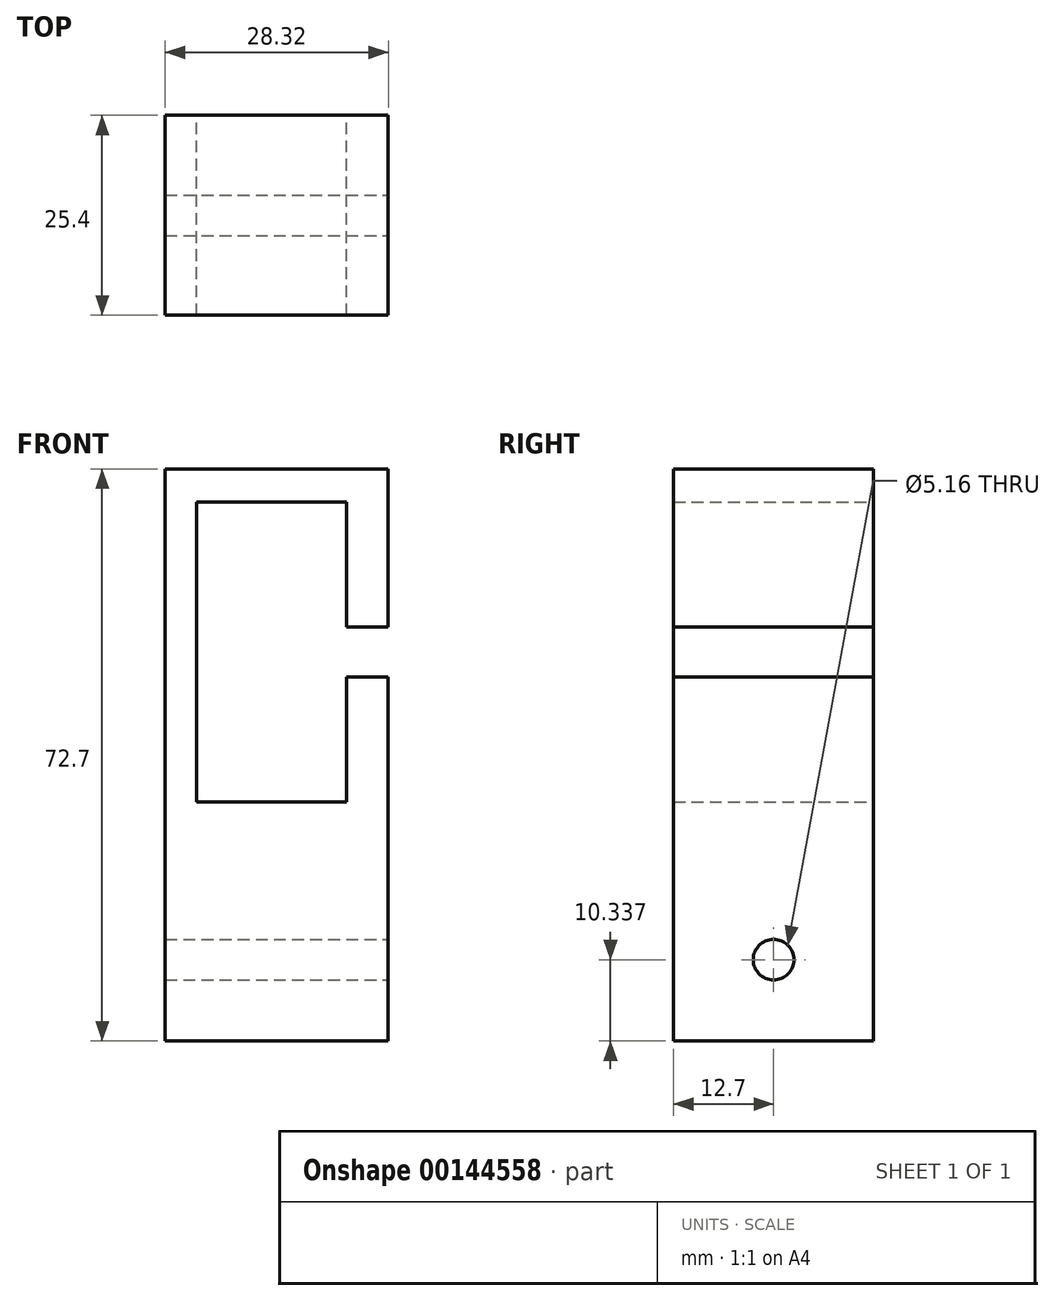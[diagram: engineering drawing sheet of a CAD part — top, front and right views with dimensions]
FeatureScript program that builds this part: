
annotation { "Feature Type Name" : "Feature", "Feature Type Description" : "" }
export const myFeature = defineFeature(function(context is Context, id is Id, definition is map)
    precondition{}
    {
        {
            var Q0;
            Q0=qCreatedBy(makeId("Front.planeOp"),FACE);
            cPlane(context, id + "F0", {"entities" : qUnion([Q0]), "cplaneType" : CPlaneType.OFFSET, "offset" : 25.4 * mm, "width" : 152.4 * mm, "height" : 152.4 * mm});
        }
        {
            var Q0;
            Q0=qCreatedBy(id+"F0.planeOp",FACE);
            var sketch = newSketch(context, id + "F1", { "sketchPlane" : qUnion([Q0])});
            skLineSegment(sketch, "E0.bottom", {"start": v(-12.7, 18.7) * mm, "end": v(6.35, 18.7) * mm});
            skLineSegment(sketch, "E0.top", {"start": v(-12.7, -19.4) * mm, "end": v(6.35, -19.4) * mm});
            skLineSegment(sketch, "E0.left", {"start": v(-12.7, 18.7) * mm, "end": v(-12.7, -19.4) * mm});
            skLineSegment(sketch, "E1", {"start": v(6.35, -3.53) * mm, "end": v(6.35, -19.4) * mm});
            skLineSegment(sketch, "E2", {"start": v(6.35, 2.82) * mm, "end": v(6.35, 18.7) * mm});
            skLineSegment(sketch, "E3", {"start": v(6.35, 2.82) * mm, "end": v(-1.27, 2.82) * mm});
            skLineSegment(sketch, "E4.bottom", {"start": v(-1.27, 2.82) * mm, "end": v(6.35, 2.82) * mm});
            skLineSegment(sketch, "E4.top", {"start": v(-1.27, -3.53) * mm, "end": v(6.35, -3.53) * mm});
            skLineSegment(sketch, "E4.left", {"start": v(-1.27, 2.82) * mm, "end": v(-1.27, -3.53) * mm});
            skLineSegment(sketch, "E5.bottom", {"start": v(-16.64, 22.92) * mm, "end": v(11.68, 22.92) * mm});
            skLineSegment(sketch, "E5.top", {"start": v(-16.64, -24.38) * mm, "end": v(11.68, -24.38) * mm});
            skLineSegment(sketch, "E5.left", {"start": v(-16.64, 22.92) * mm, "end": v(-16.64, -24.38) * mm});
            skLineSegment(sketch, "E5.right", {"start": v(11.68, 22.92) * mm, "end": v(11.68, -24.38) * mm});
            skLineSegment(sketch, "E6", {"start": v(6.35, 2.82) * mm, "end": v(11.68, 2.82) * mm});
            skLineSegment(sketch, "E7", {"start": v(6.35, -3.53) * mm, "end": v(11.68, -3.53) * mm});
            skSolve(sketch);
        }
        {
            var Q0;
            Q0=makeQuery(id+"F1.imprint","IMPRINT",FACE,{"disambiguationData":[TD([[makeQuery(id+"F1.imprint","IMPRINT",EDGE,{"derivedFrom":sQuery(id+"F1.wireOp",EDGE,"E0.bottom")}),1.0]])]});
            extrude(context, id + "F2", {"entities" : qUnion([Q0]), "depth" : 25.4 * mm});
        }
        {
            var Q0;
            Q0=makeQuery(id+"F2.opExtrude","SWEPT_FACE",FACE,{"disambiguationData":[OSD([sQuery(id+"F1.wireOp",EDGE,"E5.top")])]});
            var sketch = newSketch(context, id + "F3", { "sketchPlane" : qUnion([Q0])});
            skLineSegment(sketch, "E8", {"start": v(11.68, 50.8) * mm, "end": v(11.68, 25.4) * mm});
            skLineSegment(sketch, "E9", {"start": v(11.68, 25.4) * mm, "end": v(5.33, 25.4) * mm});
            skLineSegment(sketch, "E10", {"start": v(5.33, 25.4) * mm, "end": v(5.33, 50.8) * mm});
            skLineSegment(sketch, "E11", {"start": v(5.33, 50.8) * mm, "end": v(11.68, 50.8) * mm});
            skLineSegment(sketch, "E12", {"start": v(-16.64, 50.8) * mm, "end": v(-10.3, 50.8) * mm});
            skLineSegment(sketch, "E13", {"start": v(-10.3, 50.8) * mm, "end": v(-10.3, 25.4) * mm});
            skLineSegment(sketch, "E14", {"start": v(-10.3, 25.4) * mm, "end": v(-16.64, 25.4) * mm});
            skLineSegment(sketch, "E15", {"start": v(-16.64, 25.4) * mm, "end": v(-16.64, 50.8) * mm});
            skSolve(sketch);
        }
        {
            var Q0;
            {var subQ0=sQuery(id+"F3.wireOp",EDGE,"buzHyjwq-HXQf-YIrW-el5Z-peVdExIHBdDW.bottom");Q0=makeQuery(id+"F3.imprint","IMPRINT",FACE,{"disambiguationData":[TD([[makeQuery(id+"F3.imprint","IMPRINT",EDGE,{"derivedFrom":subQ0}),-1.0]])]});}
            var Q1;
            {var subQ0=sQuery(id+"F3.wireOp",EDGE,"WweTZzOk-0KYm-pjyf-us1Z-YU6pIId4Ppd7.left");Q1=makeQuery(id+"F3.imprint","IMPRINT",FACE,{"disambiguationData":[TD([[makeQuery(id+"F3.imprint","IMPRINT",EDGE,{"derivedFrom":subQ0}),1.0]])]});}
            var Q2;
            Q2=makeQuery(id+"F3.imprint","IMPRINT",FACE,{"disambiguationData":[TD([[makeQuery(id+"F3.imprint","IMPRINT",EDGE,{"derivedFrom":sQuery(id+"F3.wireOp",EDGE,"E12")}),-1.0]])]});
            var Q3;
            Q3=makeQuery(id+"F3.imprint","IMPRINT",FACE,{"disambiguationData":[TD([[makeQuery(id+"F3.imprint","IMPRINT",EDGE,{"derivedFrom":sQuery(id+"F3.wireOp",EDGE,"E8")}),-1.0]])]});
            var Q4;
            {var subQ0=sQuery(id+"F3.wireOp",EDGE,"E10");Q4=makeQuery(id+"F3.imprint","IMPRINT",FACE,{"disambiguationData":[TD([[makeQuery(id+"F3.imprint","IMPRINT",EDGE,{"derivedFrom":subQ0}),1.0]])]});}
            extrude(context, id + "F4", {"entities" : qUnion([Q0, Q1, Q2, Q3, Q4]), "operationType" : NewBodyOperationType.ADD, "depth" : 25.4 * mm});
        }
        {
            var Q0;
            {var subQ0=sQuery(id+"F1.wireOp",EDGE,"E5.right");Q0=makeQuery(id+"F2.opExtrude","SWEPT_FACE",FACE,{"disambiguationData":[OSD([subQ0]),TDD([makeQuery(id+"F1.imprint","IMPRINT",EDGE,{"disambiguationData":[TD([[makeQuery(id+"F1.imprint","INTERSECT",VERTEX,{"derivedFrom":[sQuery(id+"F1.wireOp",EDGE,"E5.top"),subQ0]}),1.0]])],"derivedFrom":subQ0})])]});}
            var sketch = newSketch(context, id + "F5", { "sketchPlane" : qUnion([Q0])});
            skLineSegment(sketch, "E16", {"start": v(-38.1, -3.53) * mm, "end": v(-38.1, 2.82) * mm});
            skLineSegment(sketch, "E17", {"start": v(-38.1, -0.35) * mm, "end": v(-38.1, -39.44) * mm});
            skCircle(sketch, "E18", {"center": v(-38.1, -39.44) * mm, "radius": 2.58 * mm});
            skSolve(sketch);
        }
        {
            var Q0;
            Q0=makeQuery(id+"F5.imprint","IMPRINT",FACE,{"disambiguationData":[TD([[makeQuery(id+"F5.imprint","IMPRINT",EDGE,{"derivedFrom":sQuery(id+"F5.wireOp",EDGE,"E18")}),1.0]])]});
            var Q1;
            Q1=sQuery(id+"F5.wireOp",EDGE,"E18");
            extrude(context, id + "F6", {"entities" : qUnion([Q0]), "operationType" : NewBodyOperationType.REMOVE, "surfaceEntities" : qUnion([Q1]), "oppositeDirection" : true, "depth" : 38.1 * mm});
        }
    });
